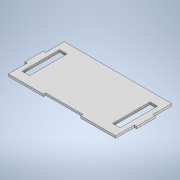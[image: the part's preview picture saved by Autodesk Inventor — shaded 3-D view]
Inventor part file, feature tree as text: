
AUTODESK INVENTOR PART (.ipt)
format: ipt  version: 2020 (Build 240168000, 168)  size: 157,184 bytes
history: native  units: in
note: dims shown in document units (in); Inventor stores cm internally (conversion verified against a paired STEP export)
features: extrude x5, sketch x5
ambient origin geometry x8: Origin, YZ Plane, XZ Plane, XY Plane, X Axis, Y Axis, Z Axis, Center Point
bodies: Solid1 (feature_tree)
feature tree (10):
  extrude  "Extrusion1"  Depth=1.9685in
  extrude  "Extrusion2"  Depth=0.1181in TaperAngle=0.0deg
  extrude  "Extrusion3"  Depth=0.1575in
  extrude  "Extrusion4"  Depth=0.1575in
  extrude  "Extrusion5"  Depth=0.1181in TaperAngle=0.0deg
  sketch  "Sketch1"  dims[d9=0.1181in d10=0.0in d13=1.9685in]
  sketch  "Sketch2"  dims[d14=0.1181in d17=1.1811in d18=0.0in]
  sketch  "Sketch3"  dims[d32=0.1575in d35=0.1575in]
  sketch  "Sketch4"  dims[d38=0.1575in d39=0.1575in]
  sketch  "Sketch5"  dims[d42=0.3937in d43=0.0in d44=0.1181in d45=0.0in d46=4.0187in d47=0.0in]
